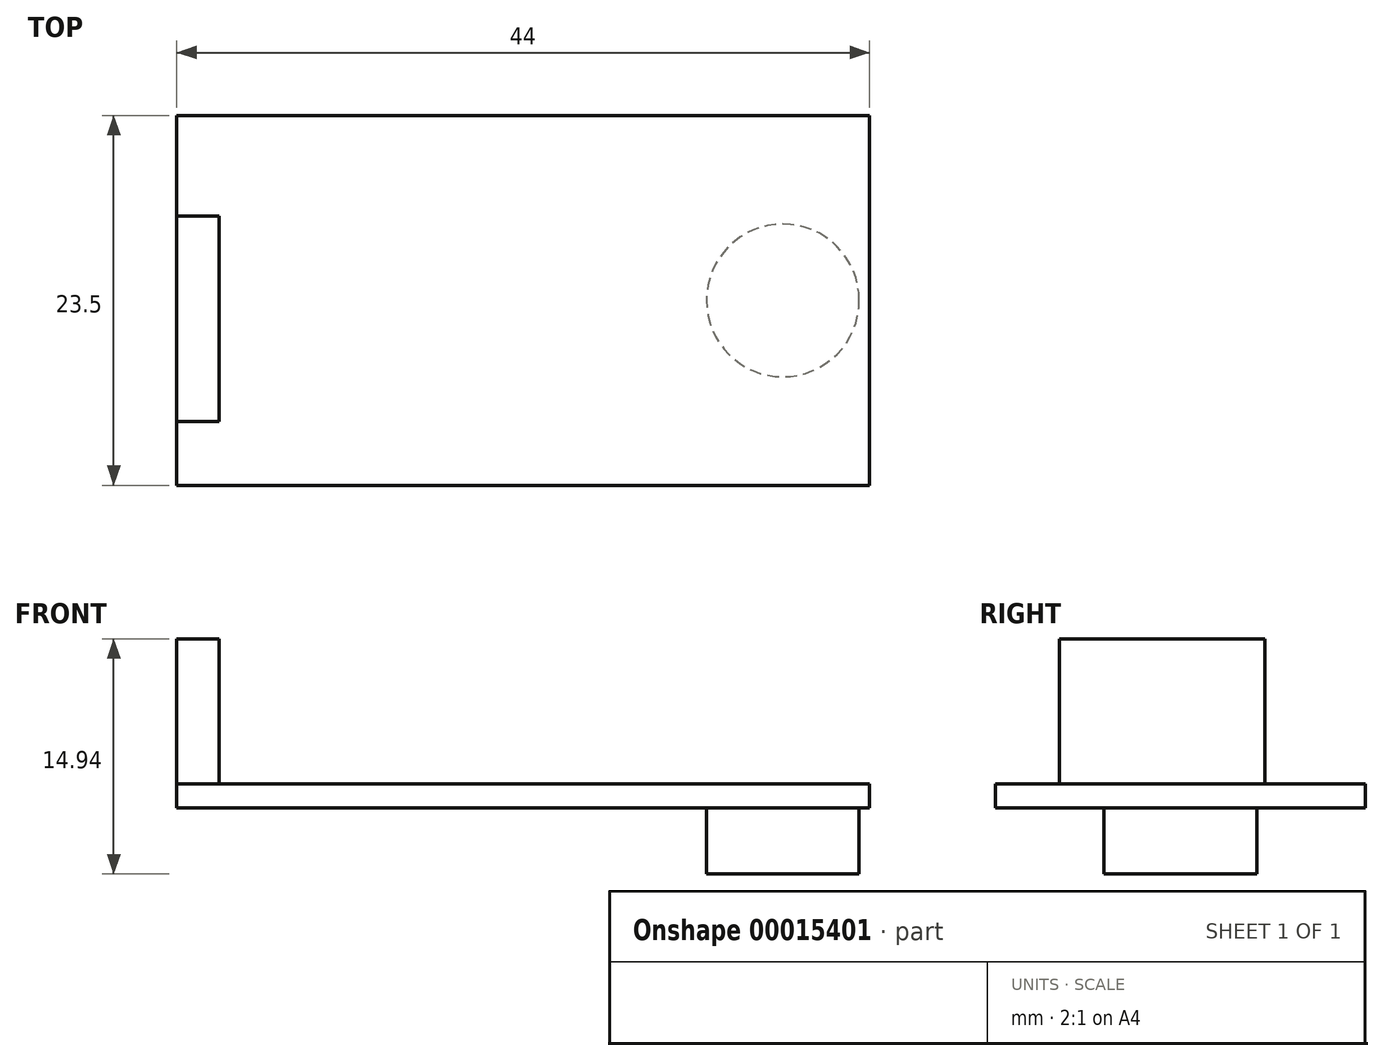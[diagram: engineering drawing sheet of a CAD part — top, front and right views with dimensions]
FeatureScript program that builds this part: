
annotation { "Feature Type Name" : "Feature", "Feature Type Description" : "" }
export const myFeature = defineFeature(function(context is Context, id is Id, definition is map)
    precondition{}
    {
        {
            var Q0;
            Q0=qCreatedBy(makeId("Top.planeOp"),FACE);
            var sketch = newSketch(context, id + "F0", { "sketchPlane" : qUnion([Q0])});
            skLineSegment(sketch, "E0.rect.bottom", {"start": v(22, -11.75) * mm, "end": v(-22, -11.75) * mm});
            skLineSegment(sketch, "E0.rect.top", {"start": v(22, 11.75) * mm, "end": v(-22, 11.75) * mm});
            skLineSegment(sketch, "E0.rect.left", {"start": v(22, -11.75) * mm, "end": v(22, 11.75) * mm});
            skLineSegment(sketch, "E0.rect.right", {"start": v(-22, -11.75) * mm, "end": v(-22, 11.75) * mm});
            skPoint(sketch, "E0.rect.middle", {"position": v(0, 0) * mm});
            skSolve(sketch);
        }
        {
            var Q0;
            Q0=makeQuery(id+"F0.imprint","IMPRINT",FACE,{"disambiguationData":[TD([[makeQuery(id+"F0.imprint","IMPRINT",EDGE,{"derivedFrom":sQuery(id+"F0.wireOp",EDGE,"E0.rect.bottom")}),-1.0]])]});
            extrude(context, id + "F1", {"entities" : qUnion([Q0]), "depth" : 1.54 * mm});
        }
        {
            var Q0;
            Q0=qCreatedBy(makeId("Top.planeOp"),FACE);
            var sketch = newSketch(context, id + "F2", { "sketchPlane" : qUnion([Q0])});
            skLineSegment(sketch, "E1", {"start": v(16.5, 11.83) * mm, "end": v(16.5, -11.69) * mm});
            skPoint(sketch, "E2", {"position": v(16.5, -5.29) * mm});
            skPoint(sketch, "E3", {"position": v(16.5, 5.43) * mm});
            skCircle(sketch, "E4", {"center": v(16.5, 0) * mm, "radius": 4.85 * mm});
            skSolve(sketch);
        }
        {
            var Q0;
            {var subQ0=sQuery(id+"F2.wireOp",EDGE,"E4");var subQ1=sQuery(id+"F2.wireOp",EDGE,"E1");var subQ3=makeQuery(id+"F2.imprint","INTERSECT",VERTEX,{"disambiguationData":[OD(0.0)],"derivedFrom":[subQ1,subQ0]});Q0=makeQuery(id+"F2.imprint","IMPRINT",FACE,{"disambiguationData":[TD([[makeQuery(id+"F2.imprint","IMPRINT",EDGE,{"disambiguationData":[TD([[subQ3,1.0]])],"derivedFrom":subQ1}),1.0]])]});}
            var Q1;
            {var subQ0=sQuery(id+"F2.wireOp",EDGE,"E4");var subQ1=sQuery(id+"F2.wireOp",EDGE,"E1");var subQ3=makeQuery(id+"F2.imprint","INTERSECT",VERTEX,{"disambiguationData":[OD(0.0)],"derivedFrom":[subQ1,subQ0]});Q1=makeQuery(id+"F2.imprint","IMPRINT",FACE,{"disambiguationData":[TD([[makeQuery(id+"F2.imprint","IMPRINT",EDGE,{"disambiguationData":[TD([[subQ3,1.0]])],"derivedFrom":subQ1}),-1.0]])]});}
            extrude(context, id + "F3", {"entities" : qUnion([Q0, Q1]), "operationType" : NewBodyOperationType.ADD, "oppositeDirection" : true, "depth" : 4.2 * mm});
        }
        {
            var Q0;
            Q0=makeQuery(id+"F1.opExtrude","CAP_FACE",FACE,{"disambiguationData":[OSD([sQuery(id+"F0.wireOp",EDGE,"E0.rect.bottom"),sQuery(id+"F0.wireOp",EDGE,"E0.rect.top"),sQuery(id+"F0.wireOp",EDGE,"E0.rect.left"),sQuery(id+"F0.wireOp",EDGE,"E0.rect.right")])],"isStart":false});
            var sketch = newSketch(context, id + "F4", { "sketchPlane" : qUnion([Q0])});
            skLineSegment(sketch, "E5", {"start": v(-22, 0) * mm, "end": v(0, 0) * mm});
            skPoint(sketch, "E6", {"position": v(-19.3, 0) * mm});
            skLineSegment(sketch, "E7", {"start": v(-20.65, -11.75) * mm, "end": v(-20.65, 11.75) * mm});
            skPoint(sketch, "E8", {"position": v(-20.65, 0) * mm});
            skPoint(sketch, "E9", {"position": v(-20.65, -7.75) * mm});
            skPoint(sketch, "E10", {"position": v(-20.65, 5.25) * mm});
            skLineSegment(sketch, "E11.bottom", {"start": v(-22, -7.7) * mm, "end": v(-19.3, -7.7) * mm});
            skLineSegment(sketch, "E11.top", {"start": v(-22, 5.36) * mm, "end": v(-19.3, 5.36) * mm});
            skLineSegment(sketch, "E11.left", {"start": v(-22, -7.7) * mm, "end": v(-22, 5.36) * mm});
            skLineSegment(sketch, "E11.right", {"start": v(-19.3, -7.7) * mm, "end": v(-19.3, 5.36) * mm});
            skSolve(sketch);
        }
        {
            var Q0;
            {var subQ0=sQuery(id+"F4.wireOp",EDGE,"E11.left");var subQ3=sQuery(id+"F4.wireOp",EDGE,"E5");var subQ4=makeQuery(id+"F4.imprint","INTERSECT",VERTEX,{"derivedFrom":[subQ3,subQ0]});Q0=makeQuery(id+"F4.imprint","IMPRINT",FACE,{"disambiguationData":[TD([[makeQuery(id+"F4.imprint","IMPRINT",EDGE,{"disambiguationData":[TD([[subQ4,-1.0]])],"derivedFrom":subQ3}),1.0]])]});}
            var Q1;
            {var subQ0=sQuery(id+"F4.wireOp",EDGE,"E11.right");var subQ1=sQuery(id+"F4.wireOp",EDGE,"E5");var subQ2=makeQuery(id+"F4.imprint","INTERSECT",VERTEX,{"derivedFrom":[subQ1,subQ0]});Q1=makeQuery(id+"F4.imprint","IMPRINT",FACE,{"disambiguationData":[TD([[makeQuery(id+"F4.imprint","IMPRINT",EDGE,{"disambiguationData":[TD([[subQ2,1.0]])],"derivedFrom":subQ1}),1.0]])]});}
            var Q2;
            {var subQ0=sQuery(id+"F4.wireOp",EDGE,"E11.left");var subQ3=sQuery(id+"F4.wireOp",EDGE,"E5");var subQ4=makeQuery(id+"F4.imprint","INTERSECT",VERTEX,{"derivedFrom":[subQ3,subQ0]});Q2=makeQuery(id+"F4.imprint","IMPRINT",FACE,{"disambiguationData":[TD([[makeQuery(id+"F4.imprint","IMPRINT",EDGE,{"disambiguationData":[TD([[subQ4,-1.0]])],"derivedFrom":subQ3}),-1.0]])]});}
            var Q3;
            {var subQ0=sQuery(id+"F4.wireOp",EDGE,"E11.right");var subQ1=sQuery(id+"F4.wireOp",EDGE,"E5");var subQ2=makeQuery(id+"F4.imprint","INTERSECT",VERTEX,{"derivedFrom":[subQ1,subQ0]});Q3=makeQuery(id+"F4.imprint","IMPRINT",FACE,{"disambiguationData":[TD([[makeQuery(id+"F4.imprint","IMPRINT",EDGE,{"disambiguationData":[TD([[subQ2,1.0]])],"derivedFrom":subQ1}),-1.0]])]});}
            extrude(context, id + "F5", {"entities" : qUnion([Q0, Q1, Q2, Q3]), "operationType" : NewBodyOperationType.ADD, "depth" : 9.2 * mm});
        }
    });
